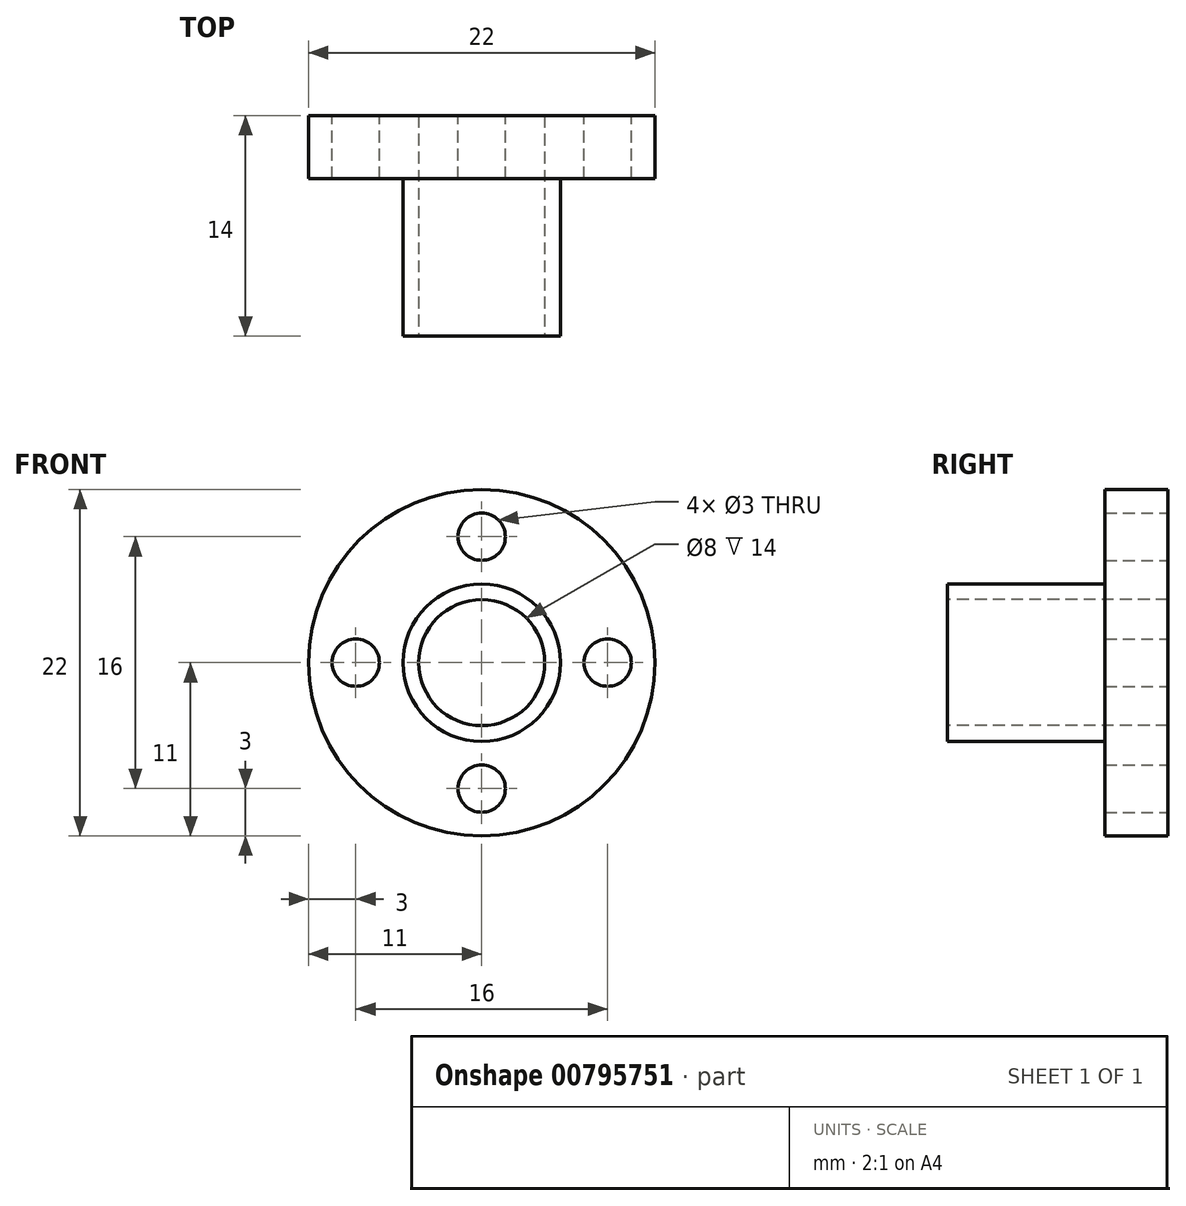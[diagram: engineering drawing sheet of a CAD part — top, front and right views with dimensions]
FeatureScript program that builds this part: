
annotation { "Feature Type Name" : "Feature", "Feature Type Description" : "" }
export const myFeature = defineFeature(function(context is Context, id is Id, definition is map)
    precondition{}
    {
        {
            var Q0;
            Q0=qCreatedBy(makeId("Front.planeOp"),FACE);
            var sketch = newSketch(context, id + "F0", { "sketchPlane" : qUnion([Q0])});
            skCircle(sketch, "E0", {"center": v(0, 0) * mm, "radius": 11 * mm});
            skSolve(sketch);
        }
        {
            var Q0;
            Q0 = qSketchRegion(id + "F0", true);
            extrude(context, id + "F1", {"entities" : qUnion([Q0]), "depth" : 4 * mm, "offsetDistance" : 25 * mm});
        }
        {
            var Q0;
            Q0=makeQuery(id+"F1.opExtrude","CAP_FACE",FACE,{"disambiguationData":[OSD([sQuery(id+"F0.wireOp",EDGE,"E0")])],"isStart":false});
            var sketch = newSketch(context, id + "F2", { "sketchPlane" : qUnion([Q0])});
            skCircle(sketch, "E1", {"center": v(0, 0) * mm, "radius": 5 * mm});
            skSolve(sketch);
        }
        {
            var Q0;
            Q0=makeQuery(id+"F2.imprint","IMPRINT",FACE,{"disambiguationData":[TD([[makeQuery(id+"F2.imprint","IMPRINT",EDGE,{"derivedFrom":sQuery(id+"F2.wireOp",EDGE,"E1")}),1.0]])]});
            var Q1;
            Q1=sQuery(id+"F2.wireOp",EDGE,"E1");
            extrude(context, id + "F3", {"entities" : qUnion([Q0]), "operationType" : NewBodyOperationType.ADD, "surfaceEntities" : qUnion([Q1]), "depth" : 10 * mm, "offsetDistance" : 25 * mm});
        }
        {
            var Q0;
            Q0=makeQuery(id+"F3.opExtrude","CAP_FACE",FACE,{"disambiguationData":[OSD([sQuery(id+"F2.wireOp",EDGE,"E1")])],"isStart":false});
            var sketch = newSketch(context, id + "F4", { "sketchPlane" : qUnion([Q0])});
            skCircle(sketch, "E2", {"center": v(0, 0) * mm, "radius": 4 * mm});
            skSolve(sketch);
        }
        {
            var Q0;
            Q0=makeQuery(id+"F4.imprint","IMPRINT",FACE,{"disambiguationData":[TD([[makeQuery(id+"F4.imprint","IMPRINT",EDGE,{"derivedFrom":sQuery(id+"F4.wireOp",EDGE,"E2")}),1.0]])]});
            extrude(context, id + "F5", {"entities" : qUnion([Q0]), "operationType" : NewBodyOperationType.REMOVE, "oppositeDirection" : true, "depth" : 25 * mm, "offsetDistance" : 25 * mm});
        }
        {
            var Q0;
            Q0=makeQuery(id+"F1.opExtrude","CAP_FACE",FACE,{"disambiguationData":[OSD([sQuery(id+"F0.wireOp",EDGE,"E0")])],"isStart":true});
            var sketch = newSketch(context, id + "F6", { "sketchPlane" : qUnion([Q0])});
            skCircle(sketch, "E3", {"center": v(0, 0) * mm, "radius": 8 * mm, "construction": true});
            skCircle(sketch, "E4", {"center": v(-8, 0) * mm, "radius": 1.5 * mm});
            skCircle(sketch, "E5.1.0", {"center": v(0, -8) * mm, "radius": 1.5 * mm});
            skCircle(sketch, "E5.2.0", {"center": v(8, 0) * mm, "radius": 1.5 * mm});
            skCircle(sketch, "E5.3.0", {"center": v(0, 8) * mm, "radius": 1.5 * mm});
            skSolve(sketch);
        }
        {
            var Q0;
            Q0=makeQuery(id+"F6.imprint","IMPRINT",FACE,{"disambiguationData":[TD([[makeQuery(id+"F6.imprint","IMPRINT",EDGE,{"derivedFrom":sQuery(id+"F6.wireOp",EDGE,"E4")}),1.0]])]});
            var Q1;
            Q1=makeQuery(id+"F6.imprint","IMPRINT",FACE,{"disambiguationData":[TD([[makeQuery(id+"F6.imprint","IMPRINT",EDGE,{"derivedFrom":sQuery(id+"F6.wireOp",EDGE,"E5.3.0")}),1.0]])]});
            var Q2;
            Q2=makeQuery(id+"F6.imprint","IMPRINT",FACE,{"disambiguationData":[TD([[makeQuery(id+"F6.imprint","IMPRINT",EDGE,{"derivedFrom":sQuery(id+"F6.wireOp",EDGE,"E5.2.0")}),1.0]])]});
            var Q3;
            Q3=makeQuery(id+"F6.imprint","IMPRINT",FACE,{"disambiguationData":[TD([[makeQuery(id+"F6.imprint","IMPRINT",EDGE,{"derivedFrom":sQuery(id+"F6.wireOp",EDGE,"E5.1.0")}),1.0]])]});
            extrude(context, id + "F7", {"entities" : qUnion([Q0, Q1, Q2, Q3]), "operationType" : NewBodyOperationType.REMOVE, "oppositeDirection" : true, "depth" : 25 * mm, "offsetDistance" : 25 * mm});
        }
    });
